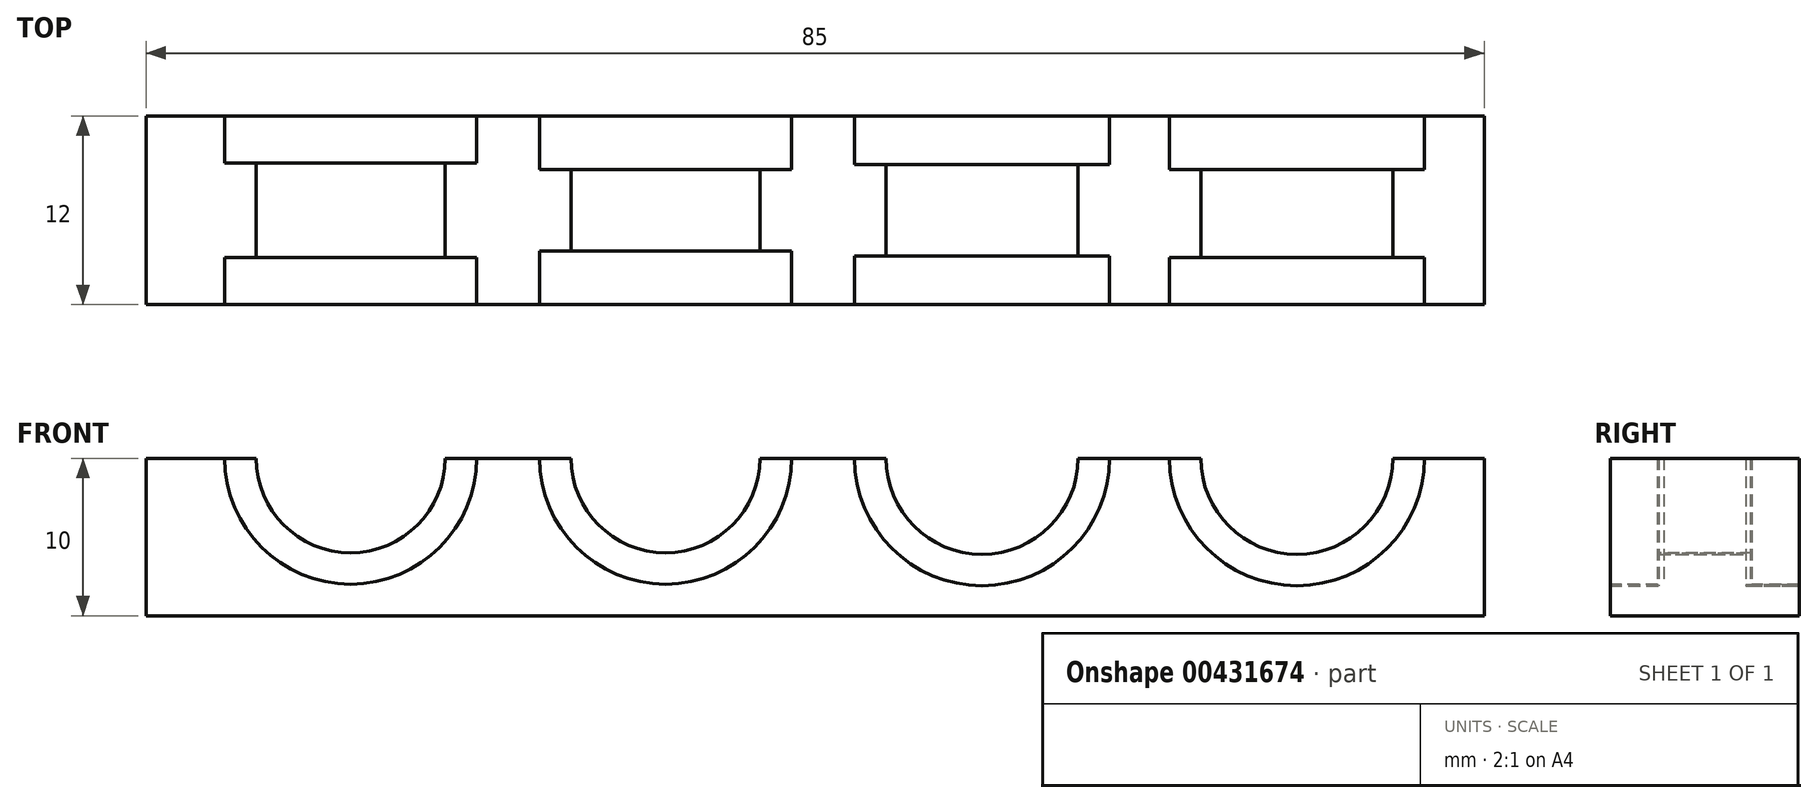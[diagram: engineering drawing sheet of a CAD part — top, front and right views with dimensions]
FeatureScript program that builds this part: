
annotation { "Feature Type Name" : "Feature", "Feature Type Description" : "" }
export const myFeature = defineFeature(function(context is Context, id is Id, definition is map)
    precondition{}
    {
        {
            var Q0;
            Q0=qCreatedBy(makeId("Top.planeOp"),FACE);
            cPlane(context, id + "F0", {"entities" : qUnion([Q0]), "cplaneType" : CPlaneType.OFFSET, "offset" : 10 * mm, "width" : 150 * mm, "height" : 150 * mm});
        }
        {
            var Q0;
            Q0=qCreatedBy(makeId("Top.planeOp"),FACE);
            var sketch = newSketch(context, id + "F1", { "sketchPlane" : qUnion([Q0])});
            skLineSegment(sketch, "E0.bottom", {"start": v(0, 0) * mm, "end": v(85, 0) * mm});
            skLineSegment(sketch, "E0.top", {"start": v(0, 12) * mm, "end": v(85, 12) * mm});
            skLineSegment(sketch, "E0.left", {"start": v(0, 0) * mm, "end": v(0, 12) * mm});
            skLineSegment(sketch, "E0.right", {"start": v(85, 0) * mm, "end": v(85, 12) * mm});
            skSolve(sketch);
        }
        {
            var Q0;
            Q0 = qSketchRegion(id + "F1", true);
            extrude(context, id + "F2", {"entities" : qUnion([Q0]), "depth" : 10 * mm});
        }
        {
            var Q0;
            Q0=qCreatedBy(id+"F0.planeOp",FACE);
            var sketch = newSketch(context, id + "F3", { "sketchPlane" : qUnion([Q0])});
            skLineSegment(sketch, "E1", {"start": v(0, 0) * mm, "end": v(5, 0) * mm, "construction": true});
            skLineSegment(sketch, "E2", {"start": v(5, 0) * mm, "end": v(5, 3) * mm});
            skLineSegment(sketch, "E3", {"start": v(5, 3) * mm, "end": v(7, 3) * mm});
            skLineSegment(sketch, "E4", {"start": v(7, 3) * mm, "end": v(7, 9) * mm});
            skLineSegment(sketch, "E5", {"start": v(7, 9) * mm, "end": v(5, 9) * mm});
            skLineSegment(sketch, "E6", {"start": v(5, 9) * mm, "end": v(5, 12) * mm});
            skLineSegment(sketch, "E7", {"start": v(5, 0) * mm, "end": v(13, 0) * mm});
            skLineSegment(sketch, "E8", {"start": v(13, 0) * mm, "end": v(13, 12) * mm});
            skLineSegment(sketch, "E9", {"start": v(5, 12) * mm, "end": v(13, 12) * mm});
            skSolve(sketch);
        }
        {
            var Q0;
            Q0 = qSketchRegion(id + "F3", true);
            var Q1;
            Q1=sQuery(id+"F3.wireOp",EDGE,"E8");
            revolve(context, id + "F4", {"operationType" : NewBodyOperationType.REMOVE, "entities" : qUnion([Q0]), "axis" : qUnion([Q1]), "revolveType" : RevolveType.FULL});
        }
        {
            var Q0;
            Q0=qCreatedBy(id+"F0.planeOp",FACE);
            var sketch = newSketch(context, id + "F5", { "sketchPlane" : qUnion([Q0])});
            skLineSegment(sketch, "E10", {"start": v(0, 0) * mm, "end": v(25, 0) * mm, "construction": true});
            skLineSegment(sketch, "E11", {"start": v(25, 0) * mm, "end": v(25, 3.4) * mm});
            skLineSegment(sketch, "E12", {"start": v(25, 3.4) * mm, "end": v(27, 3.4) * mm});
            skLineSegment(sketch, "E13", {"start": v(27, 3.4) * mm, "end": v(27, 8.6) * mm});
            skLineSegment(sketch, "E14", {"start": v(27, 8.6) * mm, "end": v(25, 8.6) * mm});
            skLineSegment(sketch, "E15", {"start": v(25, 8.6) * mm, "end": v(25, 12) * mm});
            skLineSegment(sketch, "E16", {"start": v(25, 0) * mm, "end": v(33, 0) * mm});
            skLineSegment(sketch, "E17", {"start": v(33, 0) * mm, "end": v(33, 12) * mm});
            skLineSegment(sketch, "E18", {"start": v(25, 12) * mm, "end": v(33, 12) * mm});
            skSolve(sketch);
        }
        {
            var Q0;
            Q0=makeQuery(id+"F5.imprint","IMPRINT",FACE,{"disambiguationData":[TD([[makeQuery(id+"F5.imprint","IMPRINT",EDGE,{"derivedFrom":sQuery(id+"F5.wireOp",EDGE,"E11")}),-1.0]])]});
            var Q1;
            Q1=sQuery(id+"F5.wireOp",EDGE,"E17");
            revolve(context, id + "F6", {"operationType" : NewBodyOperationType.REMOVE, "entities" : qUnion([Q0]), "axis" : qUnion([Q1]), "revolveType" : RevolveType.FULL, "oppositeDirection" : true});
        }
        {
            var Q0;
            Q0=qCreatedBy(id+"F0.planeOp",FACE);
            var sketch = newSketch(context, id + "F7", { "sketchPlane" : qUnion([Q0])});
            skLineSegment(sketch, "E19", {"start": v(0, 0) * mm, "end": v(45, 0) * mm, "construction": true});
            skLineSegment(sketch, "E20", {"start": v(45, 0) * mm, "end": v(45, 3.1) * mm});
            skLineSegment(sketch, "E21", {"start": v(45, 3.1) * mm, "end": v(47, 3.1) * mm});
            skLineSegment(sketch, "E22", {"start": v(47, 3.1) * mm, "end": v(47, 8.9) * mm});
            skLineSegment(sketch, "E23", {"start": v(47, 8.9) * mm, "end": v(45, 8.9) * mm});
            skLineSegment(sketch, "E24", {"start": v(45, 8.9) * mm, "end": v(45, 12) * mm});
            skLineSegment(sketch, "E25", {"start": v(45, 0) * mm, "end": v(53.1, 0) * mm});
            skLineSegment(sketch, "E26", {"start": v(53.1, 0) * mm, "end": v(53.1, 12) * mm});
            skLineSegment(sketch, "E27", {"start": v(45, 12) * mm, "end": v(53.1, 12) * mm});
            skSolve(sketch);
        }
        {
            var Q0;
            Q0 = qSketchRegion(id + "F7", true);
            var Q1;
            Q1=sQuery(id+"F7.wireOp",EDGE,"E26");
            revolve(context, id + "F8", {"operationType" : NewBodyOperationType.REMOVE, "entities" : qUnion([Q0]), "axis" : qUnion([Q1]), "revolveType" : RevolveType.FULL, "oppositeDirection" : true});
        }
        {
            var Q0;
            Q0=qCreatedBy(id+"F0.planeOp",FACE);
            var sketch = newSketch(context, id + "F9", { "sketchPlane" : qUnion([Q0])});
            skLineSegment(sketch, "E28", {"start": v(0, 0) * mm, "end": v(65, 0) * mm, "construction": true});
            skLineSegment(sketch, "E29", {"start": v(65, 0) * mm, "end": v(65, 3) * mm});
            skLineSegment(sketch, "E30", {"start": v(65, 3) * mm, "end": v(67, 3) * mm});
            skLineSegment(sketch, "E31", {"start": v(67, 3) * mm, "end": v(67, 8.6) * mm});
            skLineSegment(sketch, "E32", {"start": v(67, 8.6) * mm, "end": v(65, 8.6) * mm});
            skLineSegment(sketch, "E33", {"start": v(65, 8.6) * mm, "end": v(65, 12) * mm});
            skLineSegment(sketch, "E34", {"start": v(65, 0) * mm, "end": v(73.1, 0) * mm});
            skLineSegment(sketch, "E35", {"start": v(73.1, 0) * mm, "end": v(73.1, 12) * mm});
            skLineSegment(sketch, "E36", {"start": v(65, 12) * mm, "end": v(73.1, 12) * mm});
            skSolve(sketch);
        }
        {
            var Q0;
            Q0=makeQuery(id+"F9.imprint","IMPRINT",FACE,{"disambiguationData":[TD([[makeQuery(id+"F9.imprint","IMPRINT",EDGE,{"derivedFrom":sQuery(id+"F9.wireOp",EDGE,"E29")}),-1.0]])]});
            var Q1;
            Q1=sQuery(id+"F9.wireOp",EDGE,"E35");
            revolve(context, id + "F10", {"operationType" : NewBodyOperationType.REMOVE, "entities" : qUnion([Q0]), "axis" : qUnion([Q1]), "revolveType" : RevolveType.FULL, "oppositeDirection" : true});
        }
    });
